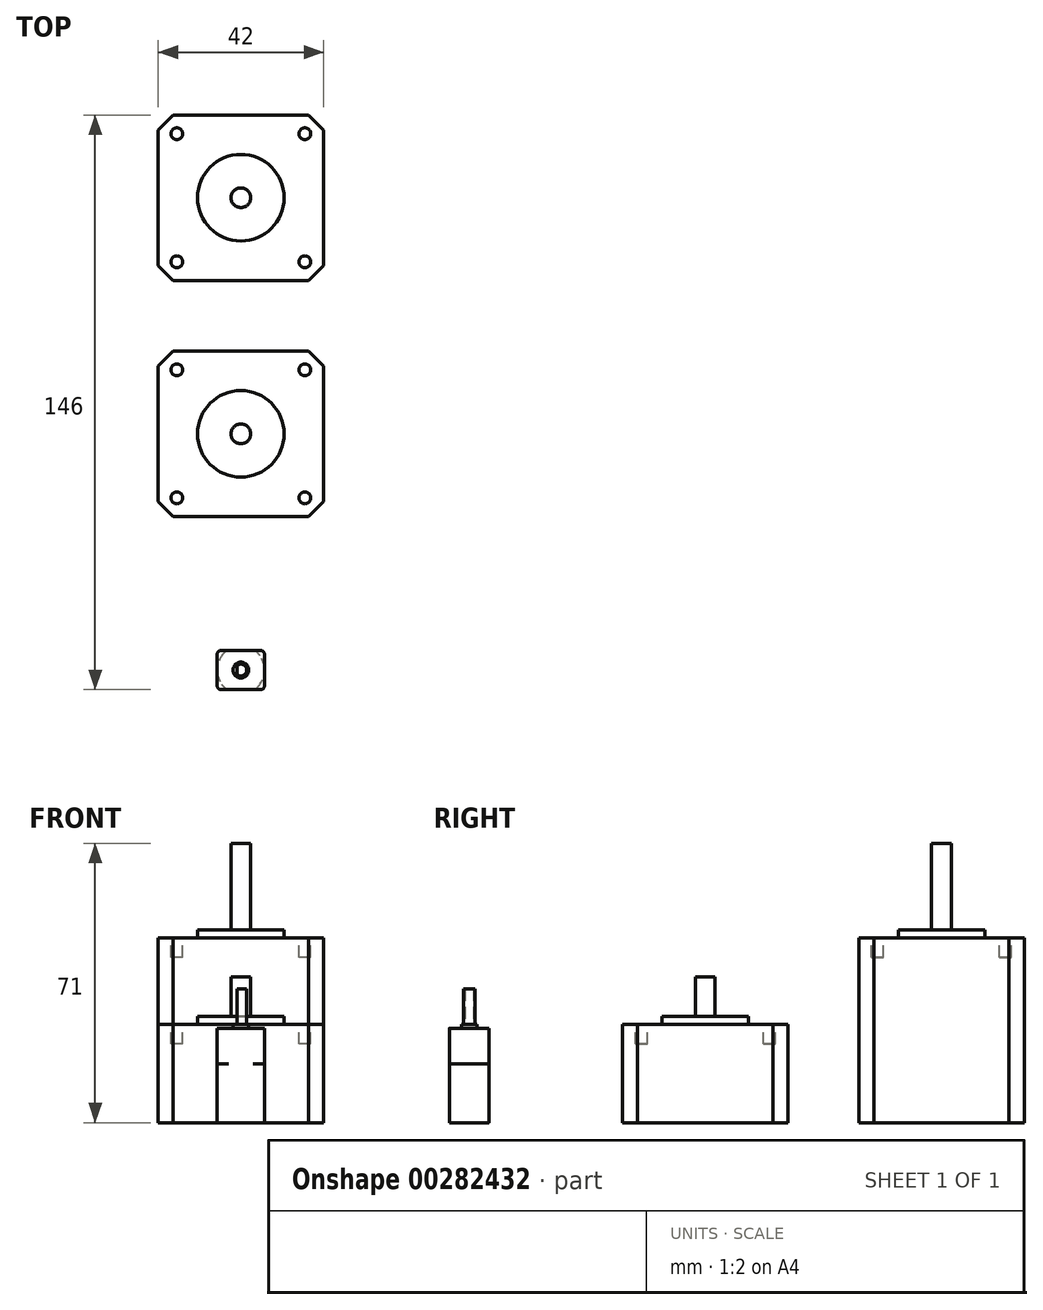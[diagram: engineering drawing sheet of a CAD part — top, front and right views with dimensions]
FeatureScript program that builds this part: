
annotation { "Feature Type Name" : "Feature", "Feature Type Description" : "" }
export const myFeature = defineFeature(function(context is Context, id is Id, definition is map)
    precondition{}
    {
        {
            var Q0;
            Q0=qCreatedBy(makeId("Front.planeOp"),FACE);
            cPlane(context, id + "F0", {"entities" : qUnion([Q0]), "cplaneType" : CPlaneType.OFFSET, "offset" : 60 * mm, "width" : 150 * mm, "height" : 150 * mm});
        }
        {
            var Q0;
            Q0=qCreatedBy(makeId("Front.planeOp"),FACE);
            cPlane(context, id + "F1", {"entities" : qUnion([Q0]), "cplaneType" : CPlaneType.OFFSET, "offset" : 120 * mm, "width" : 150 * mm, "height" : 150 * mm});
        }
        {
            var Q0;
            Q0=qCreatedBy(makeId("Top.planeOp"),FACE);
            var sketch = newSketch(context, id + "F2", { "sketchPlane" : qUnion([Q0])});
            skLineSegment(sketch, "E0", {"start": v(-21, 17.18) * mm, "end": v(-21, -17.18) * mm});
            skLineSegment(sketch, "E1", {"start": v(-21, -17.18) * mm, "end": v(-17.18, -21) * mm});
            skLineSegment(sketch, "E2", {"start": v(-17.18, -21) * mm, "end": v(17.18, -21) * mm});
            skLineSegment(sketch, "E3", {"start": v(17.18, -21) * mm, "end": v(21, -17.18) * mm});
            skLineSegment(sketch, "E4", {"start": v(21, -17.18) * mm, "end": v(21, 17.18) * mm});
            skLineSegment(sketch, "E5", {"start": v(21, 17.18) * mm, "end": v(17.18, 21) * mm});
            skLineSegment(sketch, "E6", {"start": v(17.18, 21) * mm, "end": v(-17.18, 21) * mm});
            skLineSegment(sketch, "E7", {"start": v(-17.18, 21) * mm, "end": v(-21, 17.18) * mm});
            skPoint(sketch, "E8", {"position": v(-19.1, -19.1) * mm});
            skPoint(sketch, "E9", {"position": v(19.1, 19.1) * mm});
            skLineSegment(sketch, "E10", {"start": v(-21, -42.82) * mm, "end": v(-21, -77.18) * mm});
            skLineSegment(sketch, "E11", {"start": v(-21, -77.18) * mm, "end": v(-17.18, -81) * mm});
            skLineSegment(sketch, "E12", {"start": v(-17.18, -81) * mm, "end": v(17.18, -81) * mm});
            skLineSegment(sketch, "E13", {"start": v(17.18, -81) * mm, "end": v(21, -77.18) * mm});
            skLineSegment(sketch, "E14", {"start": v(21, -77.18) * mm, "end": v(21, -42.82) * mm});
            skLineSegment(sketch, "E15", {"start": v(21, -42.82) * mm, "end": v(17.18, -39) * mm});
            skLineSegment(sketch, "E16", {"start": v(17.18, -39) * mm, "end": v(-17.18, -39) * mm});
            skLineSegment(sketch, "E17", {"start": v(-17.18, -39) * mm, "end": v(-21, -42.82) * mm});
            skPoint(sketch, "E18", {"position": v(-19.1, -79.1) * mm});
            skPoint(sketch, "E19", {"position": v(19.1, -40.9) * mm});
            skPoint(sketch, "E20", {"position": v(0, -120) * mm});
            skSolve(sketch);
        }
        {
            var Q0;
            Q0=makeQuery(id+"F2.imprint","IMPRINT",FACE,{"disambiguationData":[TD([[makeQuery(id+"F2.imprint","IMPRINT",EDGE,{"derivedFrom":sQuery(id+"F2.wireOp",EDGE,"E0")}),1.0]])]});
            extrude(context, id + "F3", {"entities" : qUnion([Q0]), "depth" : 47 * mm});
        }
        {
            var Q0;
            Q0=makeQuery(id+"F3.opExtrude","CAP_FACE",FACE,{"disambiguationData":[OSD([sQuery(id+"F2.wireOp",EDGE,"E0"),sQuery(id+"F2.wireOp",EDGE,"E1"),sQuery(id+"F2.wireOp",EDGE,"E2"),sQuery(id+"F2.wireOp",EDGE,"E3"),sQuery(id+"F2.wireOp",EDGE,"E4"),sQuery(id+"F2.wireOp",EDGE,"E5"),sQuery(id+"F2.wireOp",EDGE,"E6"),sQuery(id+"F2.wireOp",EDGE,"E7")])],"isStart":false});
            var sketch = newSketch(context, id + "F4", { "sketchPlane" : qUnion([Q0])});
            skCircle(sketch, "E21", {"center": v(0, 0) * mm, "radius": 11 * mm});
            skCircle(sketch, "E22", {"center": v(0, 0) * mm, "radius": 2.5 * mm});
            skLineSegment(sketch, "E23", {"start": v(-21, -11.53) * mm, "end": v(-11.53, -21) * mm, "construction": true});
            skCircle(sketch, "E24", {"center": v(-16.26, -16.26) * mm, "radius": 1.5 * mm});
            skCircle(sketch, "E25.1.0", {"center": v(16.26, -16.26) * mm, "radius": 1.5 * mm});
            skCircle(sketch, "E25.2.0", {"center": v(16.26, 16.26) * mm, "radius": 1.5 * mm});
            skCircle(sketch, "E25.3.0", {"center": v(-16.26, 16.26) * mm, "radius": 1.5 * mm});
            skSolve(sketch);
        }
        {
            var Q0;
            Q0=makeQuery(id+"F4.imprint","IMPRINT",FACE,{"disambiguationData":[TD([[makeQuery(id+"F4.imprint","IMPRINT",EDGE,{"derivedFrom":sQuery(id+"F4.wireOp",EDGE,"E21")}),1.0]])]});
            extrude(context, id + "F5", {"entities" : qUnion([Q0]), "operationType" : NewBodyOperationType.ADD, "depth" : 2 * mm});
        }
        {
            var Q0;
            Q0=makeQuery(id+"F5.boolean.opBoolean","SPLIT",FACE,{"disambiguationData":[TD([makeQuery(id+"F5.opExtrude","SWEPT_FACE",FACE,{"disambiguationData":[OSD([sQuery(id+"F4.wireOp",EDGE,"E22")])]})])],"derivedFrom":makeQuery(id+"F3.opExtrude","CAP_FACE",FACE,{"disambiguationData":[OSD([sQuery(id+"F2.wireOp",EDGE,"E0"),sQuery(id+"F2.wireOp",EDGE,"E1"),sQuery(id+"F2.wireOp",EDGE,"E2"),sQuery(id+"F2.wireOp",EDGE,"E3"),sQuery(id+"F2.wireOp",EDGE,"E4"),sQuery(id+"F2.wireOp",EDGE,"E5"),sQuery(id+"F2.wireOp",EDGE,"E6"),sQuery(id+"F2.wireOp",EDGE,"E7")])],"isStart":false})});
            extrude(context, id + "F6", {"entities" : qUnion([Q0]), "operationType" : NewBodyOperationType.ADD, "depth" : (2 + 22) * mm});
        }
        {
            var Q0;
            Q0=makeQuery(id+"F4.imprint","IMPRINT",FACE,{"disambiguationData":[TD([[makeQuery(id+"F4.imprint","IMPRINT",EDGE,{"derivedFrom":sQuery(id+"F4.wireOp",EDGE,"E25.1.0")}),1.0]])]});
            var Q1;
            Q1=makeQuery(id+"F4.imprint","IMPRINT",FACE,{"disambiguationData":[TD([[makeQuery(id+"F4.imprint","IMPRINT",EDGE,{"derivedFrom":sQuery(id+"F4.wireOp",EDGE,"E25.2.0")}),1.0]])]});
            var Q2;
            Q2=makeQuery(id+"F4.imprint","IMPRINT",FACE,{"disambiguationData":[TD([[makeQuery(id+"F4.imprint","IMPRINT",EDGE,{"derivedFrom":sQuery(id+"F4.wireOp",EDGE,"E25.3.0")}),1.0]])]});
            var Q3;
            Q3=makeQuery(id+"F4.imprint","IMPRINT",FACE,{"disambiguationData":[TD([[makeQuery(id+"F4.imprint","IMPRINT",EDGE,{"derivedFrom":sQuery(id+"F4.wireOp",EDGE,"E24")}),1.0]])]});
            extrude(context, id + "F7", {"entities" : qUnion([Q0, Q1, Q2, Q3]), "operationType" : NewBodyOperationType.REMOVE, "oppositeDirection" : true, "depth" : 5 * mm});
        }
        {
            var Q0;
            Q0=makeQuery(id+"F2.imprint","IMPRINT",FACE,{"disambiguationData":[TD([[makeQuery(id+"F2.imprint","IMPRINT",EDGE,{"derivedFrom":sQuery(id+"F2.wireOp",EDGE,"E10")}),1.0]])]});
            extrude(context, id + "F8", {"entities" : qUnion([Q0]), "depth" : 25 * mm});
        }
        {
            var Q0;
            Q0=makeQuery(id+"F8.opExtrude","CAP_FACE",FACE,{"disambiguationData":[OSD([sQuery(id+"F2.wireOp",EDGE,"E10"),sQuery(id+"F2.wireOp",EDGE,"E11"),sQuery(id+"F2.wireOp",EDGE,"E12"),sQuery(id+"F2.wireOp",EDGE,"E13"),sQuery(id+"F2.wireOp",EDGE,"E14"),sQuery(id+"F2.wireOp",EDGE,"E15"),sQuery(id+"F2.wireOp",EDGE,"E16"),sQuery(id+"F2.wireOp",EDGE,"E17")])],"isStart":false});
            var sketch = newSketch(context, id + "F9", { "sketchPlane" : qUnion([Q0])});
            skCircle(sketch, "E26", {"center": v(0, -60) * mm, "radius": 11 * mm});
            skCircle(sketch, "E27", {"center": v(0, -60) * mm, "radius": 2.5 * mm});
            skLineSegment(sketch, "E28", {"start": v(-21, -71.53) * mm, "end": v(-11.53, -81) * mm, "construction": true});
            skCircle(sketch, "E29", {"center": v(-16.26, -76.26) * mm, "radius": 1.5 * mm});
            skCircle(sketch, "E30.1.0", {"center": v(16.26, -76.26) * mm, "radius": 1.5 * mm});
            skCircle(sketch, "E30.2.0", {"center": v(16.26, -43.74) * mm, "radius": 1.5 * mm});
            skCircle(sketch, "E30.3.0", {"center": v(-16.26, -43.74) * mm, "radius": 1.5 * mm});
            skSolve(sketch);
        }
        {
            var Q0;
            Q0=makeQuery(id+"F9.imprint","IMPRINT",FACE,{"disambiguationData":[TD([[makeQuery(id+"F9.imprint","IMPRINT",EDGE,{"derivedFrom":sQuery(id+"F9.wireOp",EDGE,"E29")}),1.0]])]});
            var Q1;
            Q1=makeQuery(id+"F9.imprint","IMPRINT",FACE,{"disambiguationData":[TD([[makeQuery(id+"F9.imprint","IMPRINT",EDGE,{"derivedFrom":sQuery(id+"F9.wireOp",EDGE,"E30.1.0")}),1.0]])]});
            var Q2;
            Q2=makeQuery(id+"F9.imprint","IMPRINT",FACE,{"disambiguationData":[TD([[makeQuery(id+"F9.imprint","IMPRINT",EDGE,{"derivedFrom":sQuery(id+"F9.wireOp",EDGE,"E30.2.0")}),1.0]])]});
            var Q3;
            Q3=makeQuery(id+"F9.imprint","IMPRINT",FACE,{"disambiguationData":[TD([[makeQuery(id+"F9.imprint","IMPRINT",EDGE,{"derivedFrom":sQuery(id+"F9.wireOp",EDGE,"E30.3.0")}),1.0]])]});
            extrude(context, id + "F10", {"entities" : qUnion([Q0, Q1, Q2, Q3]), "operationType" : NewBodyOperationType.REMOVE, "oppositeDirection" : true, "depth" : 5 * mm});
        }
        {
            var Q0;
            Q0=makeQuery(id+"F9.imprint","IMPRINT",FACE,{"disambiguationData":[TD([[makeQuery(id+"F9.imprint","IMPRINT",EDGE,{"derivedFrom":sQuery(id+"F9.wireOp",EDGE,"E26")}),1.0]])]});
            extrude(context, id + "F11", {"entities" : qUnion([Q0]), "operationType" : NewBodyOperationType.ADD, "depth" : 2 * mm});
        }
        {
            var Q0;
            Q0=makeQuery(id+"F9.imprint","IMPRINT",FACE,{"disambiguationData":[TD([[makeQuery(id+"F9.imprint","IMPRINT",EDGE,{"derivedFrom":sQuery(id+"F9.wireOp",EDGE,"E27")}),1.0]])]});
            extrude(context, id + "F12", {"entities" : qUnion([Q0]), "operationType" : NewBodyOperationType.ADD, "depth" : (2 + 10) * mm});
        }
        {
            var Q0;
            Q0=qCreatedBy(makeId("Top.planeOp"),FACE);
            var sketch = newSketch(context, id + "F13", { "sketchPlane" : qUnion([Q0])});
            skLineSegment(sketch, "E31", {"start": v(-3.5, -115) * mm, "end": v(3.5, -115) * mm});
            skArc(sketch, "E32", {"start": v(-3.5, -115) * mm, "mid": v(-6, -120) * mm, "end": v(-3.5, -125) * mm});
            skArc(sketch, "E33", {"start": v(3.5, -115) * mm, "mid": v(6, -120) * mm, "end": v(3.5, -125) * mm});
            skLineSegment(sketch, "E34", {"start": v(-3.5, -125) * mm, "end": v(3.5, -125) * mm});
            skPoint(sketch, "E35", {"position": v(-6, -120) * mm});
            skPoint(sketch, "E36", {"position": v(6, -120) * mm});
            skSolve(sketch);
        }
        {
            var Q0;
            Q0=makeQuery(id+"F13.imprint","IMPRINT",FACE,{"disambiguationData":[TD([[makeQuery(id+"F13.imprint","IMPRINT",EDGE,{"derivedFrom":sQuery(id+"F13.wireOp",EDGE,"E31")}),-1.0]])]});
            extrude(context, id + "F14", {"entities" : qUnion([Q0]), "depth" : 15 * mm});
        }
        {
            var Q0;
            Q0=makeQuery(id+"F14.opExtrude","CAP_FACE",FACE,{"disambiguationData":[OSD([sQuery(id+"F13.wireOp",EDGE,"E31"),sQuery(id+"F13.wireOp",EDGE,"E32"),sQuery(id+"F13.wireOp",EDGE,"E33"),sQuery(id+"F13.wireOp",EDGE,"E34")])],"isStart":false});
            var sketch = newSketch(context, id + "F15", { "sketchPlane" : qUnion([Q0])});
            skLineSegment(sketch, "E37.bottom", {"start": v(6, -125) * mm, "end": v(-6, -125) * mm});
            skLineSegment(sketch, "E37.top", {"start": v(6, -115) * mm, "end": v(-6, -115) * mm});
            skLineSegment(sketch, "E37.left", {"start": v(6, -125) * mm, "end": v(6, -115) * mm});
            skLineSegment(sketch, "E37.right", {"start": v(-6, -125) * mm, "end": v(-6, -115) * mm});
            skPoint(sketch, "E37.middle", {"position": v(0, -120) * mm});
            skSolve(sketch);
        }
        {
            var Q0;
            {var subQ0=sQuery(id+"F15.wireOp",EDGE,"E37.bottom");var subQ1=makeQuery(id+"F14.opExtrude","CAP_EDGE",EDGE,{"disambiguationData":[OSD([sQuery(id+"F13.wireOp",EDGE,"E32")])],"isStart":false});var subQ2=makeQuery(id+"F15.imprint","INTERSECT",VERTEX,{"derivedFrom":[subQ1,subQ0]});var subQ3=sQuery(id+"F15.wireOp",EDGE,"E37.right");var subQ4=makeQuery(id+"F15.imprint","INTERSECT",VERTEX,{"derivedFrom":[subQ0,subQ3]});Q0=makeQuery(id+"F15.imprint","IMPRINT",FACE,{"disambiguationData":[TD([[makeQuery(id+"F15.imprint","IMPRINT",EDGE,{"disambiguationData":[TD([[subQ2,-1.0],[subQ4,1.0]])],"derivedFrom":subQ0}),-1.0]])]});}
            var Q1;
            {var subQ0=sQuery(id+"F15.wireOp",EDGE,"E37.top");var subQ1=makeQuery(id+"F14.opExtrude","CAP_EDGE",EDGE,{"disambiguationData":[OSD([sQuery(id+"F13.wireOp",EDGE,"E32")])],"isStart":false});var subQ2=makeQuery(id+"F15.imprint","INTERSECT",VERTEX,{"derivedFrom":[subQ1,subQ0]});var subQ3=sQuery(id+"F15.wireOp",EDGE,"E37.right");var subQ4=makeQuery(id+"F15.imprint","INTERSECT",VERTEX,{"derivedFrom":[subQ0,subQ3]});Q1=makeQuery(id+"F15.imprint","IMPRINT",FACE,{"disambiguationData":[TD([[makeQuery(id+"F15.imprint","IMPRINT",EDGE,{"disambiguationData":[TD([[subQ2,-1.0],[subQ4,1.0]])],"derivedFrom":subQ0}),1.0]])]});}
            var Q2;
            {var subQ1=makeQuery(id+"F14.opExtrude","CAP_EDGE",EDGE,{"disambiguationData":[OSD([sQuery(id+"F13.wireOp",EDGE,"E32")])],"isStart":false});var subQ4=makeQuery(id+"F14.opExtrude","CAP_EDGE",EDGE,{"disambiguationData":[OSD([sQuery(id+"F13.wireOp",EDGE,"E33")])],"isStart":false});var subQ6=sQuery(id+"F15.wireOp",EDGE,"E37.bottom");var subQ7=makeQuery(id+"F15.imprint","INTERSECT",VERTEX,{"derivedFrom":[subQ1,subQ6]});var subQ8=makeQuery(id+"F15.imprint","INTERSECT",VERTEX,{"derivedFrom":[subQ4,subQ6]});Q2=makeQuery(id+"F15.imprint","IMPRINT",FACE,{"disambiguationData":[TD([[makeQuery(id+"F15.imprint","IMPRINT",EDGE,{"disambiguationData":[TD([[subQ7,-1.0],[subQ8,1.0]])],"derivedFrom":subQ6}),1.0]])]});}
            var Q3;
            {var subQ0=sQuery(id+"F15.wireOp",EDGE,"E37.top");var subQ1=makeQuery(id+"F14.opExtrude","CAP_EDGE",EDGE,{"disambiguationData":[OSD([sQuery(id+"F13.wireOp",EDGE,"E33")])],"isStart":false});var subQ2=makeQuery(id+"F15.imprint","INTERSECT",VERTEX,{"derivedFrom":[subQ1,subQ0]});var subQ3=sQuery(id+"F15.wireOp",EDGE,"E37.left");var subQ4=makeQuery(id+"F15.imprint","INTERSECT",VERTEX,{"derivedFrom":[subQ0,subQ3]});Q3=makeQuery(id+"F15.imprint","IMPRINT",FACE,{"disambiguationData":[TD([[makeQuery(id+"F15.imprint","IMPRINT",EDGE,{"disambiguationData":[TD([[subQ2,1.0],[subQ4,-1.0]])],"derivedFrom":subQ0}),1.0]])]});}
            var Q4;
            {var subQ0=sQuery(id+"F15.wireOp",EDGE,"E37.bottom");var subQ1=makeQuery(id+"F14.opExtrude","CAP_EDGE",EDGE,{"disambiguationData":[OSD([sQuery(id+"F13.wireOp",EDGE,"E33")])],"isStart":false});var subQ2=makeQuery(id+"F15.imprint","INTERSECT",VERTEX,{"derivedFrom":[subQ1,subQ0]});var subQ3=sQuery(id+"F15.wireOp",EDGE,"E37.left");var subQ4=makeQuery(id+"F15.imprint","INTERSECT",VERTEX,{"derivedFrom":[subQ0,subQ3]});Q4=makeQuery(id+"F15.imprint","IMPRINT",FACE,{"disambiguationData":[TD([[makeQuery(id+"F15.imprint","IMPRINT",EDGE,{"disambiguationData":[TD([[subQ2,1.0],[subQ4,-1.0]])],"derivedFrom":subQ0}),-1.0]])]});}
            extrude(context, id + "F16", {"entities" : qUnion([Q0, Q1, Q2, Q3, Q4]), "operationType" : NewBodyOperationType.ADD, "depth" : 9 * mm});
        }
        {
            var Q0;
            Q0=makeQuery(id+"F16.opExtrude","CAP_FACE",FACE,{"disambiguationData":[OSD([sQuery(id+"F15.wireOp",EDGE,"E37.bottom"),sQuery(id+"F15.wireOp",EDGE,"E37.top"),sQuery(id+"F15.wireOp",EDGE,"E37.left"),sQuery(id+"F15.wireOp",EDGE,"E37.right")])],"isStart":false});
            var sketch = newSketch(context, id + "F17", { "sketchPlane" : qUnion([Q0])});
            skCircle(sketch, "E38", {"center": v(0, -120) * mm, "radius": 2 * mm});
            skArc(sketch, "E39", {"start": v(-1, -118.88) * mm, "mid": v(1.5, -120) * mm, "end": v(-1, -121.12) * mm});
            skLineSegment(sketch, "E40", {"start": v(-1, -118.88) * mm, "end": v(-1, -121.12) * mm});
            skSolve(sketch);
        }
        {
            var Q0;
            Q0=makeQuery(id+"F17.imprint","IMPRINT",FACE,{"disambiguationData":[TD([[makeQuery(id+"F17.imprint","IMPRINT",EDGE,{"derivedFrom":sQuery(id+"F17.wireOp",EDGE,"E38")}),1.0]])]});
            extrude(context, id + "F18", {"entities" : qUnion([Q0]), "operationType" : NewBodyOperationType.ADD, "depth" : 1 * mm});
        }
        {
            var Q0;
            Q0=makeQuery(id+"F18.boolean.opBoolean","SPLIT",FACE,{"disambiguationData":[TD([makeQuery(id+"F18.opExtrude","SWEPT_FACE",FACE,{"disambiguationData":[OSD([sQuery(id+"F17.wireOp",EDGE,"E39")])]})])],"derivedFrom":makeQuery(id+"F16.opExtrude","CAP_FACE",FACE,{"disambiguationData":[OSD([sQuery(id+"F15.wireOp",EDGE,"E37.bottom"),sQuery(id+"F15.wireOp",EDGE,"E37.top"),sQuery(id+"F15.wireOp",EDGE,"E37.left"),sQuery(id+"F15.wireOp",EDGE,"E37.right")])],"isStart":false})});
            extrude(context, id + "F19", {"entities" : qUnion([Q0]), "operationType" : NewBodyOperationType.ADD, "depth" : (1 + 9) * mm});
        }
        {
            var Q0;
            Q0=makeQuery(id+"F16.opExtrude","SWEPT_EDGE",EDGE,{"disambiguationData":[OSD([sQuery(id+"F15.wireOp",EDGE,"E37.bottom"),sQuery(id+"F15.wireOp",EDGE,"E37.left")])]});
            var Q1;
            Q1=makeQuery(id+"F16.opExtrude","SWEPT_EDGE",EDGE,{"disambiguationData":[OSD([sQuery(id+"F15.wireOp",EDGE,"E37.top"),sQuery(id+"F15.wireOp",EDGE,"E37.left")])]});
            var Q2;
            Q2=makeQuery(id+"F16.opExtrude","SWEPT_EDGE",EDGE,{"disambiguationData":[OSD([sQuery(id+"F15.wireOp",EDGE,"E37.top"),sQuery(id+"F15.wireOp",EDGE,"E37.right")])]});
            var Q3;
            Q3=makeQuery(id+"F16.opExtrude","SWEPT_EDGE",EDGE,{"disambiguationData":[OSD([sQuery(id+"F15.wireOp",EDGE,"E37.bottom"),sQuery(id+"F15.wireOp",EDGE,"E37.right")])]});
            fillet(context, id + "F20", {"entities" : qUnion([Q0, Q1, Q2, Q3]), "radius" : 1 * mm, "tangentPropagation" : true, "allowEdgeOverflow" : false});
        }
        {
            var Q0;
            Q0=makeQuery(id+"F14.opExtrude","SWEPT_EDGE",EDGE,{"disambiguationData":[OSD([sQuery(id+"F13.wireOp",EDGE,"E33"),sQuery(id+"F13.wireOp",EDGE,"E34")])]});
            var Q1;
            Q1=makeQuery(id+"F14.opExtrude","SWEPT_EDGE",EDGE,{"disambiguationData":[OSD([sQuery(id+"F13.wireOp",EDGE,"E32"),sQuery(id+"F13.wireOp",EDGE,"E34")])]});
            var Q2;
            Q2=makeQuery(id+"F14.opExtrude","SWEPT_EDGE",EDGE,{"disambiguationData":[OSD([sQuery(id+"F13.wireOp",EDGE,"E31"),sQuery(id+"F13.wireOp",EDGE,"E33")])]});
            var Q3;
            Q3=makeQuery(id+"F14.opExtrude","SWEPT_EDGE",EDGE,{"disambiguationData":[OSD([sQuery(id+"F13.wireOp",EDGE,"E31"),sQuery(id+"F13.wireOp",EDGE,"E32")])]});
            fillet(context, id + "F21", {"entities" : qUnion([Q0, Q1, Q2, Q3]), "radius" : 1 * mm, "tangentPropagation" : true, "allowEdgeOverflow" : false});
        }
    });
